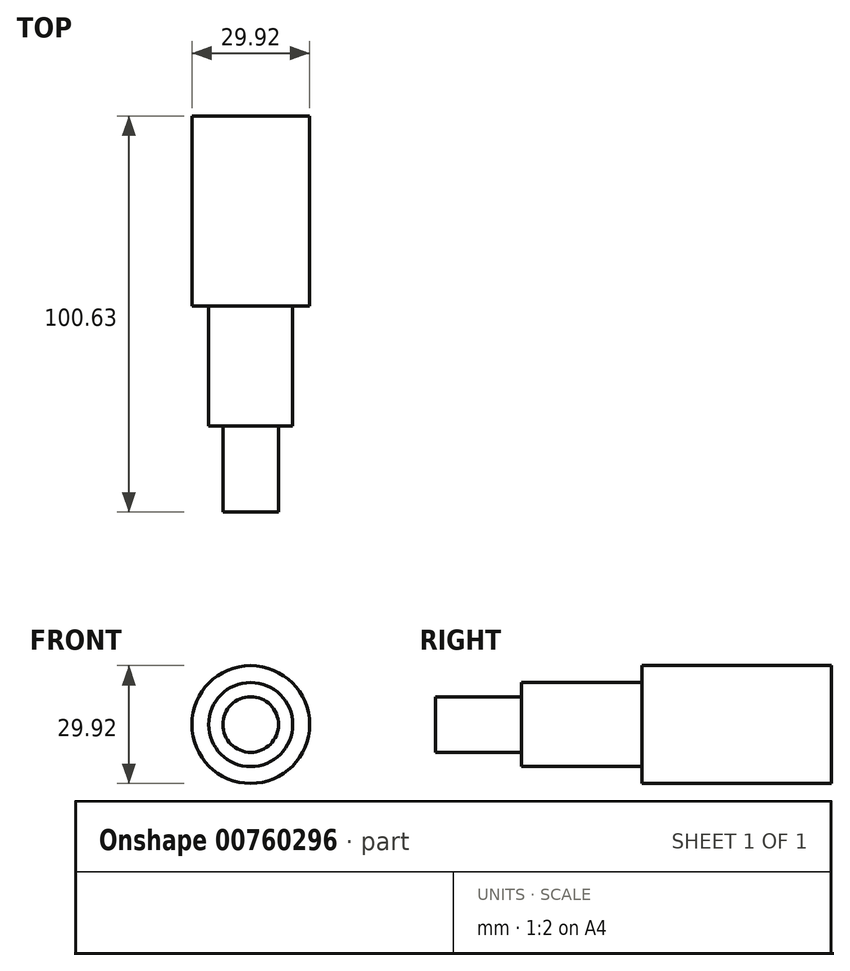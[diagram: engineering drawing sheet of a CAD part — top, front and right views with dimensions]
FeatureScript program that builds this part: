
annotation { "Feature Type Name" : "Feature", "Feature Type Description" : "" }
export const myFeature = defineFeature(function(context is Context, id is Id, definition is map)
    precondition{}
    {
        {
            var Q0;
            Q0=qCreatedBy(makeId("Front.planeOp"),FACE);
            var sketch = newSketch(context, id + "F0", { "sketchPlane" : qUnion([Q0])});
            skCircle(sketch, "E0", {"center": v(0, 0) * mm, "radius": 7.06 * mm});
            skSolve(sketch);
        }
        {
            var Q0;
            Q0=makeQuery(id+"F0.imprint","IMPRINT",FACE,{"disambiguationData":[TD([[makeQuery(id+"F0.imprint","IMPRINT",EDGE,{"derivedFrom":sQuery(id+"F0.wireOp",EDGE,"E0")}),1.0]])]});
            extrude(context, id + "F1", {"entities" : qUnion([Q0]), "oppositeDirection" : true, "depth" : 21.87 * mm, "offsetDistance" : 25.4 * mm});
        }
        {
            var Q0;
            Q0=makeQuery(id+"F1.opExtrude","CAP_FACE",FACE,{"disambiguationData":[OSD([sQuery(id+"F0.wireOp",EDGE,"E0")])],"isStart":false});
            cPlane(context, id + "F2", {"entities" : qUnion([Q0]), "cplaneType" : CPlaneType.OFFSET, "offset" : 0 * mm, "width" : 152.4 * mm, "height" : 152.4 * mm});
        }
        {
            var Q0;
            Q0=qCreatedBy(id+"F2.planeOp",FACE);
            var sketch = newSketch(context, id + "F3", { "sketchPlane" : qUnion([Q0])});
            skCircle(sketch, "E1", {"center": v(0, 0) * mm, "radius": 10.68 * mm});
            skSolve(sketch);
        }
        {
            var Q0;
            Q0=makeQuery(id+"F3.imprint","IMPRINT",FACE,{"disambiguationData":[TD([[makeQuery(id+"F3.imprint","IMPRINT",EDGE,{"derivedFrom":sQuery(id+"F3.wireOp",EDGE,"E1")}),1.0]])]});
            extrude(context, id + "F4", {"entities" : qUnion([Q0]), "operationType" : NewBodyOperationType.ADD, "depth" : 30.56 * mm, "offsetDistance" : 25.4 * mm});
        }
        {
            var Q0;
            Q0=makeQuery(id+"F4.opExtrude","CAP_FACE",FACE,{"disambiguationData":[OSD([sQuery(id+"F3.wireOp",EDGE,"E1")])],"isStart":false});
            cPlane(context, id + "F5", {"entities" : qUnion([Q0]), "cplaneType" : CPlaneType.OFFSET, "offset" : 0 * mm, "width" : 152.4 * mm, "height" : 152.4 * mm});
        }
        {
            var Q0;
            Q0=qCreatedBy(id+"F5.planeOp",FACE);
            var sketch = newSketch(context, id + "F6", { "sketchPlane" : qUnion([Q0])});
            skCircle(sketch, "E2", {"center": v(0, 0) * mm, "radius": 14.96 * mm});
            skSolve(sketch);
        }
        {
            var Q0;
            Q0=makeQuery(id+"F6.imprint","IMPRINT",FACE,{"disambiguationData":[TD([[makeQuery(id+"F6.imprint","IMPRINT",EDGE,{"derivedFrom":sQuery(id+"F6.wireOp",EDGE,"E2")}),1.0]])]});
            extrude(context, id + "F7", {"entities" : qUnion([Q0]), "operationType" : NewBodyOperationType.ADD, "depth" : 48.2 * mm, "offsetDistance" : 25.4 * mm});
        }
    });
